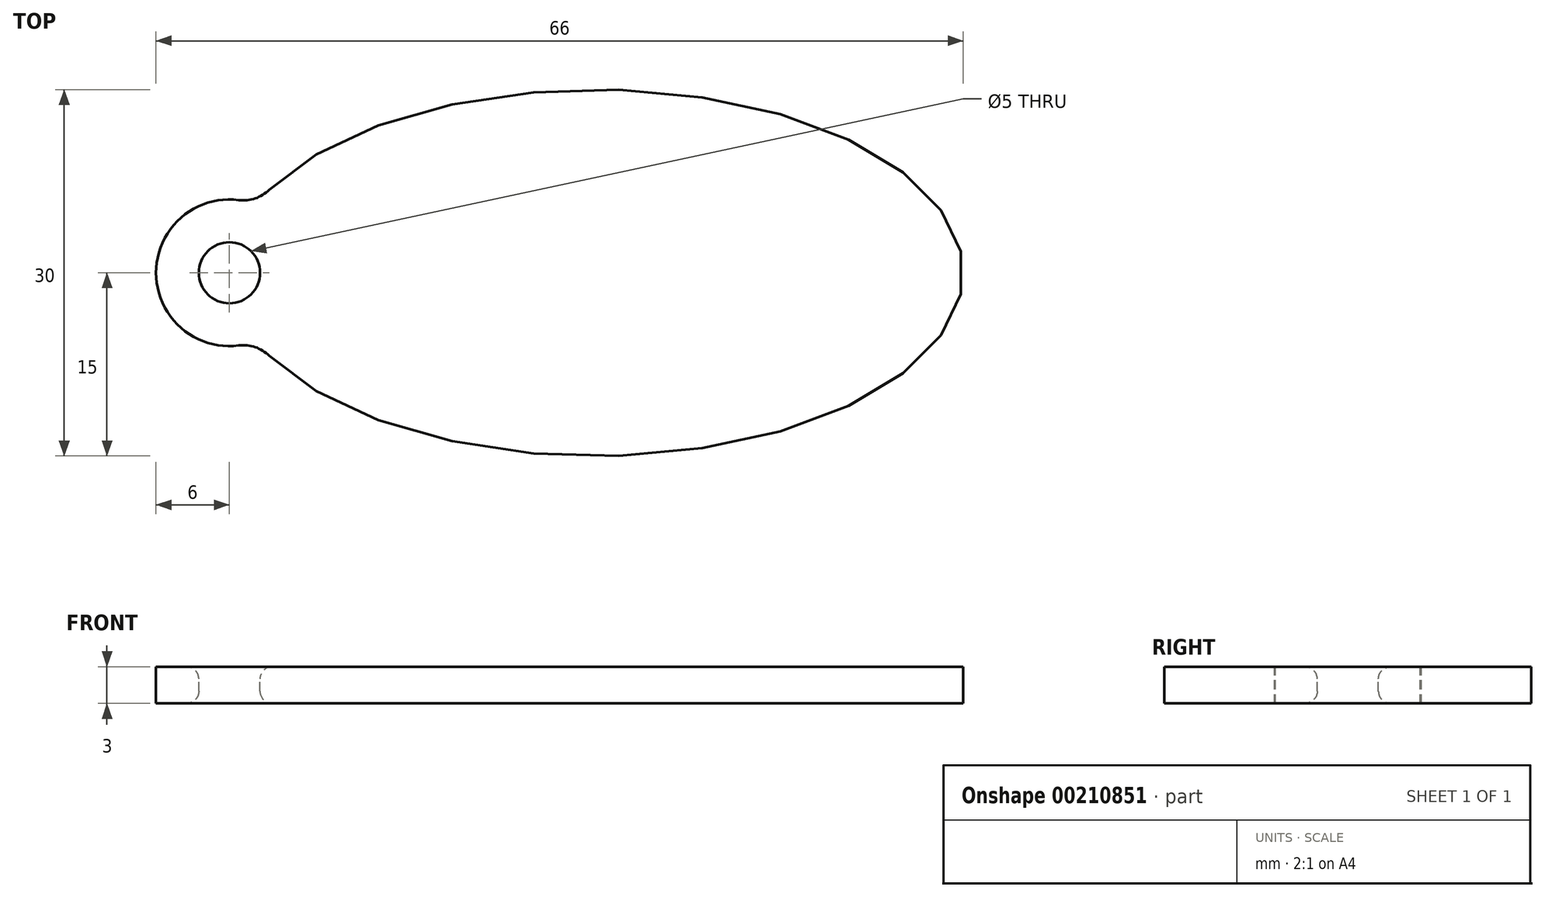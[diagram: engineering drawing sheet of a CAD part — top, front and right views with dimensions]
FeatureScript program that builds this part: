
annotation { "Feature Type Name" : "Feature", "Feature Type Description" : "" }
export const myFeature = defineFeature(function(context is Context, id is Id, definition is map)
    precondition{}
    {
        {
            var Q0;
            Q0=qCreatedBy(makeId("Top.planeOp"),FACE);
            var sketch = newSketch(context, id + "F0", { "sketchPlane" : qUnion([Q0])});
            skText(sketch, "E0", { "text": "ADINA", "fontName": "Tinos-Bold.ttf"});
            const initialGuessF0  = {"E0": [-0.025, -0.00455, 1, 0, 0.0108]};
            skSetInitialGuess(sketch, initialGuessF0);
            skSolve(sketch);
        }
        {
            var Q0;
            Q0=qCreatedBy(makeId("Top.planeOp"),FACE);
            var sketch = newSketch(context, id + "F1", { "sketchPlane" : qUnion([Q0])});
            skEllipse(sketch, "E1", {"center": v(0, 0) * mm, "majorRadius": 30 * mm, "minorRadius": 15 * mm, "majorAxis": v(1, 0)});
            skCircle(sketch, "E2", {"center": v(-30, 0) * mm, "radius": 6 * mm});
            skFitSpline(sketch, "E3.0", {"points": [v(27.43, -1) * mm, v(27.53, 0) * mm, v(27.43, 1) * mm, v(27.13, 2) * mm, v(26.6, 3.06) * mm, v(25.83, 4.14) * mm, v(24.8, 5.24) * mm, v(23.5, 6.33) * mm, v(22.2, 7.2) * mm, v(21.04, 7.88) * mm, v(20.1, 8.37) * mm, v(19.11, 8.85) * mm, v(17.73, 9.44) * mm, v(15.88, 10.13) * mm, v(13.5, 10.84) * mm, v(11, 11.43) * mm, v(8.36, 11.9) * mm, v(5.64, 12.24) * mm, v(3.32, 12.42) * mm, v(1.43, 12.49) * mm, v(0, 12.5) * mm, v(-1.43, 12.49) * mm, v(-3.32, 12.42) * mm, v(-5.64, 12.24) * mm, v(-8.36, 11.9) * mm, v(-11, 11.43) * mm, v(-13.5, 10.84) * mm, v(-15.88, 10.13) * mm, v(-17.73, 9.44) * mm, v(-19.11, 8.85) * mm, v(-20.1, 8.37) * mm, v(-21.04, 7.88) * mm, v(-22.2, 7.2) * mm, v(-23.5, 6.33) * mm, v(-24.8, 5.24) * mm, v(-25.83, 4.14) * mm, v(-26.6, 3.06) * mm, v(-27.13, 2) * mm, v(-27.43, 1) * mm, v(-27.53, 0) * mm, v(-27.43, -1) * mm, v(-27.13, -2) * mm, v(-26.6, -3.06) * mm, v(-25.83, -4.14) * mm, v(-24.8, -5.24) * mm, v(-23.5, -6.33) * mm, v(-22.2, -7.2) * mm, v(-21.04, -7.88) * mm, v(-20.1, -8.37) * mm, v(-19.11, -8.85) * mm, v(-17.73, -9.44) * mm, v(-15.88, -10.13) * mm, v(-13.5, -10.84) * mm, v(-11, -11.43) * mm, v(-8.36, -11.9) * mm, v(-5.64, -12.24) * mm, v(-3.32, -12.42) * mm, v(-1.43, -12.49) * mm, v(0, -12.5) * mm, v(1.43, -12.49) * mm, v(3.32, -12.42) * mm, v(5.64, -12.24) * mm, v(8.36, -11.9) * mm, v(11, -11.43) * mm, v(13.5, -10.84) * mm, v(15.88, -10.13) * mm, v(17.73, -9.44) * mm, v(19.11, -8.85) * mm, v(20.1, -8.37) * mm, v(21.04, -7.88) * mm, v(22.2, -7.2) * mm, v(23.5, -6.33) * mm, v(24.8, -5.24) * mm, v(25.83, -4.14) * mm, v(26.6, -3.06) * mm, v(27.13, -2) * mm, v(27.43, -1) * mm, v(27.53, 0) * mm, v(27.43, 1) * mm, v(27.43, -1) * mm]});
            skCircle(sketch, "E4", {"center": v(-30, 0) * mm, "radius": 2.5 * mm});
            skSolve(sketch);
        }
        {
            var Q0;
            {var subQ0=sQuery(id+"F1.wireOp",EDGE,"E2");var subQ1=sQuery(id+"F1.wireOp",EDGE,"E1");var subQ2=makeQuery(id+"F1.imprint","INTERSECT",VERTEX,{"disambiguationData":[OD(0.0)],"derivedFrom":[subQ1,subQ0]});Q0=makeQuery(id+"F1.imprint","IMPRINT",FACE,{"disambiguationData":[TD([[makeQuery(id+"F1.imprint","IMPRINT",EDGE,{"disambiguationData":[TD([[subQ2,1.0]])],"derivedFrom":subQ1}),1.0]])]});}
            var Q1;
            {var subQ0=sQuery(id+"F1.wireOp",EDGE,"E3.0");var subQ1=sQuery(id+"F1.wireOp",EDGE,"E2");var subQ2=makeQuery(id+"F1.imprint","INTERSECT",VERTEX,{"disambiguationData":[OD(0.0)],"derivedFrom":[subQ1,subQ0]});Q1=makeQuery(id+"F1.imprint","IMPRINT",FACE,{"disambiguationData":[TD([[makeQuery(id+"F1.imprint","IMPRINT",EDGE,{"disambiguationData":[TD([[subQ2,1.0]])],"derivedFrom":subQ1}),-1.0]])]});}
            var Q2;
            {var subQ0=sQuery(id+"F1.wireOp",EDGE,"E3.0");var subQ1=sQuery(id+"F1.wireOp",EDGE,"E2");var subQ2=makeQuery(id+"F1.imprint","INTERSECT",VERTEX,{"disambiguationData":[OD(0.0)],"derivedFrom":[subQ1,subQ0]});Q2=makeQuery(id+"F1.imprint","IMPRINT",FACE,{"disambiguationData":[TD([[makeQuery(id+"F1.imprint","IMPRINT",EDGE,{"disambiguationData":[TD([[subQ2,1.0]])],"derivedFrom":subQ1}),1.0]])]});}
            var Q3;
            {var subQ0=sQuery(id+"F1.wireOp",EDGE,"E2");var subQ1=sQuery(id+"F1.wireOp",EDGE,"E1");var subQ2=makeQuery(id+"F1.imprint","INTERSECT",VERTEX,{"disambiguationData":[OD(0.0)],"derivedFrom":[subQ1,subQ0]});Q3=makeQuery(id+"F1.imprint","IMPRINT",FACE,{"disambiguationData":[TD([[makeQuery(id+"F1.imprint","IMPRINT",EDGE,{"disambiguationData":[TD([[subQ2,-1.0]])],"derivedFrom":subQ1}),-1.0]])]});}
            var Q4;
            {var subQ0=sQuery(id+"F1.wireOp",EDGE,"E2");var subQ1=sQuery(id+"F1.wireOp",EDGE,"E1");var subQ2=makeQuery(id+"F1.imprint","INTERSECT",VERTEX,{"disambiguationData":[OD(0.0)],"derivedFrom":[subQ1,subQ0]});Q4=makeQuery(id+"F1.imprint","IMPRINT",FACE,{"disambiguationData":[TD([[makeQuery(id+"F1.imprint","IMPRINT",EDGE,{"disambiguationData":[TD([[subQ2,-1.0]])],"derivedFrom":subQ1}),1.0]])]});}
            var Q5;
            {var subQ0=sQuery(id+"F1.wireOp",EDGE,"E2");var subQ1=sQuery(id+"F1.wireOp",EDGE,"E1");var subQ2=makeQuery(id+"F1.imprint","INTERSECT",VERTEX,{"disambiguationData":[OD(1.0)],"derivedFrom":[subQ1,subQ0]});Q5=makeQuery(id+"F1.imprint","IMPRINT",FACE,{"disambiguationData":[TD([[makeQuery(id+"F1.imprint","IMPRINT",EDGE,{"disambiguationData":[TD([[subQ2,1.0]])],"derivedFrom":subQ1}),1.0]])]});}
            extrude(context, id + "F2", {"entities" : qUnion([Q0, Q1, Q2, Q3, Q4, Q5]), "oppositeDirection" : true, "depth" : 1.5 * mm, "offsetDistance" : 25 * mm});
        }
        {
            var Q0;
            {var subQ0=sQuery(id+"F1.wireOp",EDGE,"E2");var subQ1=sQuery(id+"F1.wireOp",EDGE,"E1");var subQ2=makeQuery(id+"F1.imprint","INTERSECT",VERTEX,{"disambiguationData":[OD(0.0)],"derivedFrom":[subQ1,subQ0]});Q0=makeQuery(id+"F1.imprint","IMPRINT",FACE,{"disambiguationData":[TD([[makeQuery(id+"F1.imprint","IMPRINT",EDGE,{"disambiguationData":[TD([[subQ2,1.0]])],"derivedFrom":subQ1}),1.0]])]});}
            var Q1;
            {var subQ0=sQuery(id+"F1.wireOp",EDGE,"E2");var subQ1=sQuery(id+"F1.wireOp",EDGE,"E1");var subQ2=makeQuery(id+"F1.imprint","INTERSECT",VERTEX,{"disambiguationData":[OD(0.0)],"derivedFrom":[subQ1,subQ0]});Q1=makeQuery(id+"F1.imprint","IMPRINT",FACE,{"disambiguationData":[TD([[makeQuery(id+"F1.imprint","IMPRINT",EDGE,{"disambiguationData":[TD([[subQ2,-1.0]])],"derivedFrom":subQ1}),-1.0]])]});}
            var Q2;
            {var subQ0=sQuery(id+"F1.wireOp",EDGE,"E3.0");var subQ1=sQuery(id+"F1.wireOp",EDGE,"E2");var subQ2=makeQuery(id+"F1.imprint","INTERSECT",VERTEX,{"disambiguationData":[OD(0.0)],"derivedFrom":[subQ1,subQ0]});Q2=makeQuery(id+"F1.imprint","IMPRINT",FACE,{"disambiguationData":[TD([[makeQuery(id+"F1.imprint","IMPRINT",EDGE,{"disambiguationData":[TD([[subQ2,1.0]])],"derivedFrom":subQ1}),1.0]])]});}
            var Q3;
            {var subQ0=sQuery(id+"F1.wireOp",EDGE,"E2");var subQ1=sQuery(id+"F1.wireOp",EDGE,"E1");var subQ2=makeQuery(id+"F1.imprint","INTERSECT",VERTEX,{"disambiguationData":[OD(0.0)],"derivedFrom":[subQ1,subQ0]});Q3=makeQuery(id+"F1.imprint","IMPRINT",FACE,{"disambiguationData":[TD([[makeQuery(id+"F1.imprint","IMPRINT",EDGE,{"disambiguationData":[TD([[subQ2,-1.0]])],"derivedFrom":subQ1}),1.0]])]});}
            var Q4;
            {var subQ0=sQuery(id+"F1.wireOp",EDGE,"E2");var subQ1=sQuery(id+"F1.wireOp",EDGE,"E1");var subQ2=makeQuery(id+"F1.imprint","INTERSECT",VERTEX,{"disambiguationData":[OD(1.0)],"derivedFrom":[subQ1,subQ0]});Q4=makeQuery(id+"F1.imprint","IMPRINT",FACE,{"disambiguationData":[TD([[makeQuery(id+"F1.imprint","IMPRINT",EDGE,{"disambiguationData":[TD([[subQ2,1.0]])],"derivedFrom":subQ1}),1.0]])]});}
            var Q5;
            Q5=qSketchRegion(id+"F0",true);
            extrude(context, id + "F3", {"entities" : qUnion([Q0, Q1, Q2, Q3, Q4, Q5]), "operationType" : NewBodyOperationType.ADD, "depth" : 1.5 * mm, "offsetDistance" : 25 * mm});
        }
        {
            var Q0;
            Q0=makeQuery(id+"F3.opExtrude","CAP_EDGE",EDGE,{"disambiguationData":[OSD([sQuery(id+"F1.wireOp",EDGE,"E4")])],"isStart":false});
            var Q1;
            Q1=makeQuery(id+"F2.opExtrude","CAP_EDGE",EDGE,{"disambiguationData":[OSD([sQuery(id+"F1.wireOp",EDGE,"E4")])],"isStart":false});
            fillet(context, id + "F4", {"entities" : qUnion([Q0, Q1]), "radius" : 1 * mm, "tangentPropagation" : true, "allowEdgeOverflow" : false});
        }
        {
            var Q0;
            {var subQ0=sQuery(id+"F1.wireOp",EDGE,"E2");var subQ1=sQuery(id+"F1.wireOp",EDGE,"E1");var subQ2=makeQuery(id+"F1.imprint","INTERSECT",VERTEX,{"disambiguationData":[OD(0.0)],"derivedFrom":[subQ1,subQ0]});Q0=makeQuery(id+"F3.boolean.opBoolean","MERGE",EDGE,{"derivedFrom":[makeQuery(id+"F2.opExtrude","SWEPT_EDGE",EDGE,{"disambiguationData":[OSD([subQ1,subQ0]),TDD([subQ2])]}),makeQuery(id+"F3.opExtrude","SWEPT_EDGE",EDGE,{"disambiguationData":[OSD([subQ1,subQ0]),TDD([subQ2])]})]});}
            var Q1;
            {var subQ0=sQuery(id+"F1.wireOp",EDGE,"E2");var subQ1=sQuery(id+"F1.wireOp",EDGE,"E1");var subQ2=makeQuery(id+"F1.imprint","INTERSECT",VERTEX,{"disambiguationData":[OD(1.0)],"derivedFrom":[subQ1,subQ0]});Q1=makeQuery(id+"F3.boolean.opBoolean","MERGE",EDGE,{"derivedFrom":[makeQuery(id+"F2.opExtrude","SWEPT_EDGE",EDGE,{"disambiguationData":[OSD([subQ1,subQ0]),TDD([subQ2])]}),makeQuery(id+"F3.opExtrude","SWEPT_EDGE",EDGE,{"disambiguationData":[OSD([subQ1,subQ0]),TDD([subQ2])]})]});}
            fillet(context, id + "F5", {"entities" : qUnion([Q0, Q1]), "tangentPropagation" : true, "radius" : 3 * mm, "defaultsChanged" : true, "vertexSettings" : [], "allowEdgeOverflow" : false});
        }
    });
